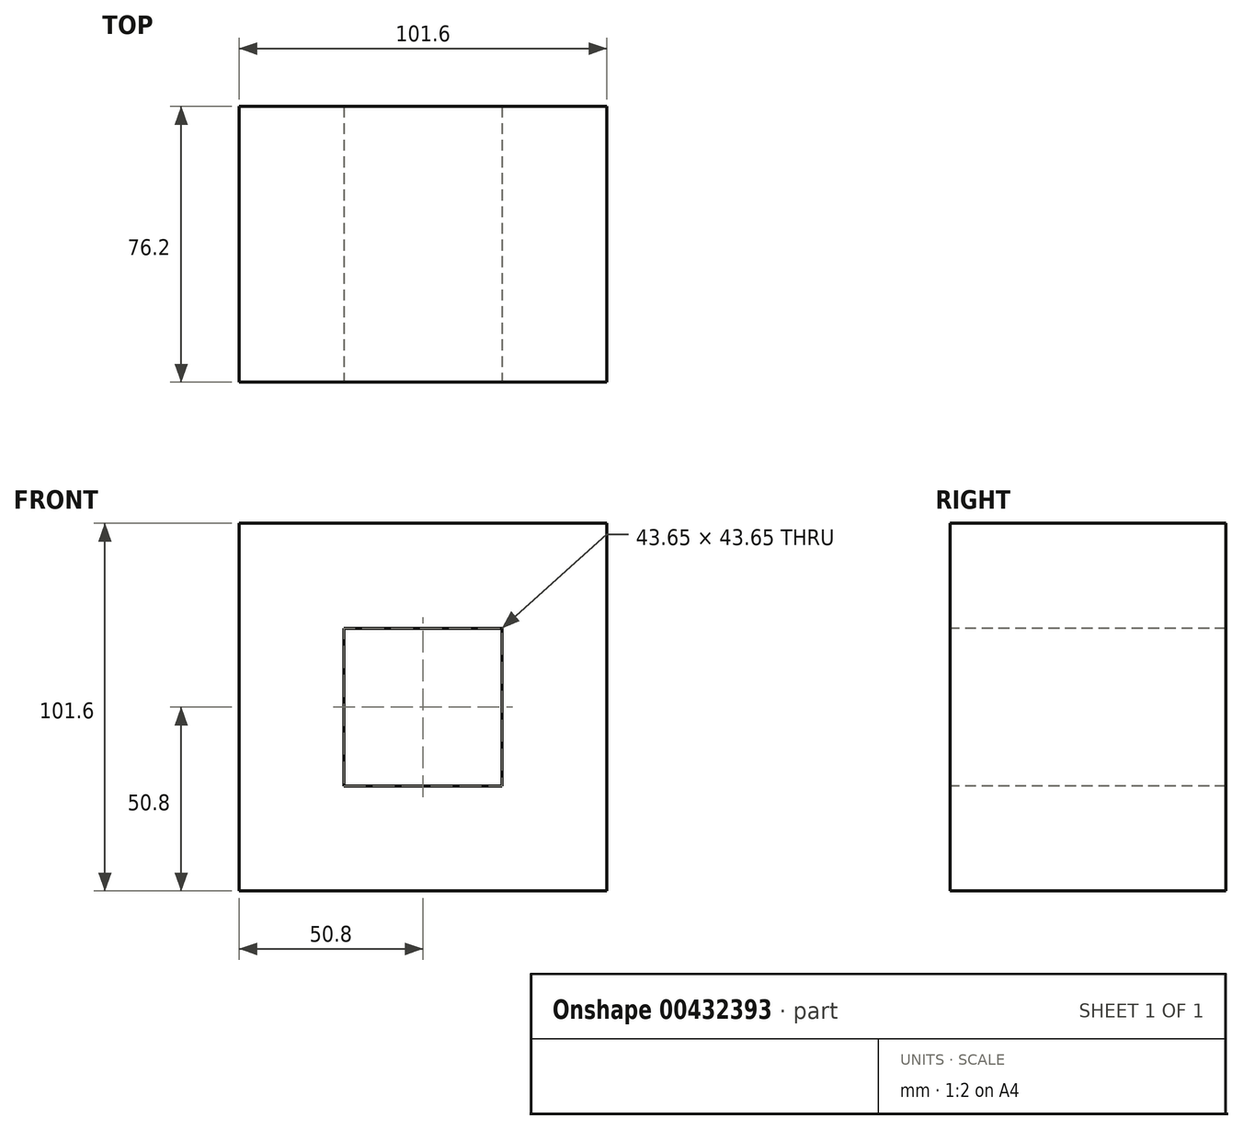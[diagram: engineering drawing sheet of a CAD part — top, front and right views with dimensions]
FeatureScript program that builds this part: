
annotation { "Feature Type Name" : "Feature", "Feature Type Description" : "" }
export const myFeature = defineFeature(function(context is Context, id is Id, definition is map)
    precondition{}
    {
        {
            var Q0;
            Q0=qCreatedBy(makeId("Front.planeOp"),FACE);
            var sketch = newSketch(context, id + "F0", { "sketchPlane" : qUnion([Q0])});
            skLineSegment(sketch, "E0.bottom", {"start": v(50.8, -50.8) * mm, "end": v(-50.8, -50.8) * mm});
            skLineSegment(sketch, "E0.top", {"start": v(50.8, 50.8) * mm, "end": v(-50.8, 50.8) * mm});
            skLineSegment(sketch, "E0.left", {"start": v(50.8, -50.8) * mm, "end": v(50.8, 50.8) * mm});
            skLineSegment(sketch, "E0.right", {"start": v(-50.8, -50.8) * mm, "end": v(-50.8, 50.8) * mm});
            skPoint(sketch, "E0.middle", {"position": v(0, 0) * mm});
            skSolve(sketch);
        }
        {
            var Q0;
            Q0=makeQuery(id+"F0.imprint","IMPRINT",FACE,{"disambiguationData":[TD([[makeQuery(id+"F0.imprint","IMPRINT",EDGE,{"derivedFrom":sQuery(id+"F0.wireOp",EDGE,"E0.bottom")}),-1.0]])]});
            extrude(context, id + "F1", {"entities" : qUnion([Q0]), "depth" : 76.2 * mm});
        }
        {
            var Q0;
            Q0=makeQuery(id+"F1.opExtrude","CAP_FACE",FACE,{"disambiguationData":[OSD([sQuery(id+"F0.wireOp",EDGE,"E0.bottom"),sQuery(id+"F0.wireOp",EDGE,"E0.top"),sQuery(id+"F0.wireOp",EDGE,"E0.left"),sQuery(id+"F0.wireOp",EDGE,"E0.right")])],"isStart":false});
            var sketch = newSketch(context, id + "F2", { "sketchPlane" : qUnion([Q0])});
            skLineSegment(sketch, "E1.bottom", {"start": v(-21.83, -21.83) * mm, "end": v(21.83, -21.83) * mm});
            skLineSegment(sketch, "E1.top", {"start": v(-21.83, 21.83) * mm, "end": v(21.83, 21.83) * mm});
            skLineSegment(sketch, "E1.left", {"start": v(-21.83, -21.83) * mm, "end": v(-21.83, 21.83) * mm});
            skLineSegment(sketch, "E1.right", {"start": v(21.83, -21.83) * mm, "end": v(21.83, 21.83) * mm});
            skPoint(sketch, "E1.middle", {"position": v(0, 0) * mm});
            skSolve(sketch);
        }
        {
            var Q0;
            Q0 = qSketchRegion(id + "F2", true);
            extrude(context, id + "F3", {"entities" : qUnion([Q0]), "operationType" : NewBodyOperationType.REMOVE, "endBound" : BoundingType.THROUGH_ALL, "oppositeDirection" : true, "depth" : 82.04 * mm});
        }
    });
